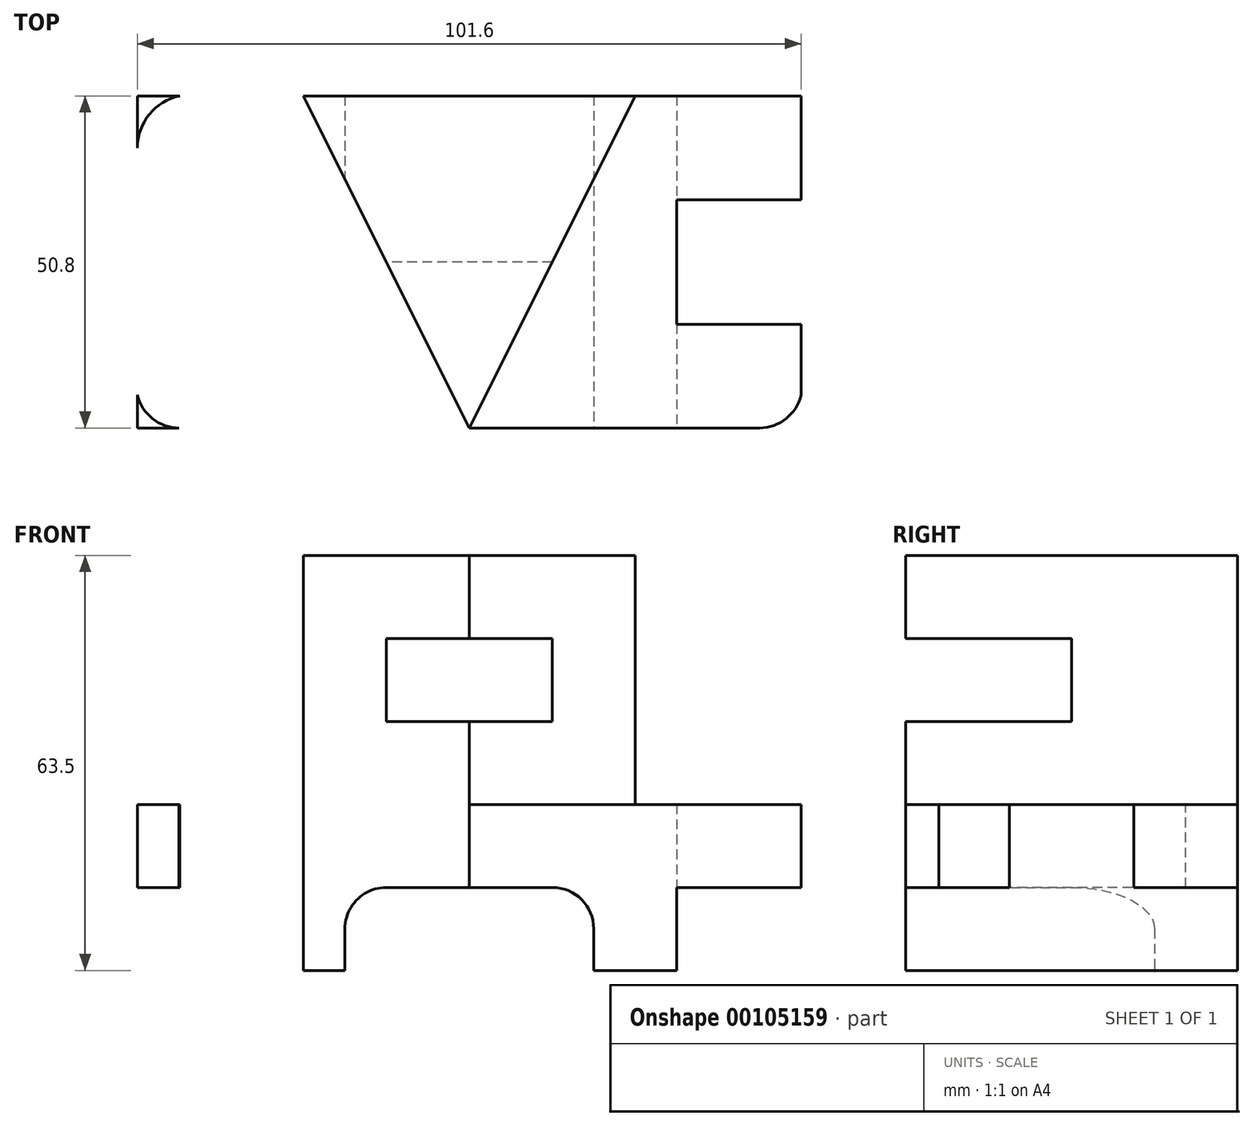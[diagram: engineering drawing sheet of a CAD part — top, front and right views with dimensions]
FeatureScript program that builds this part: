
annotation { "Feature Type Name" : "Feature", "Feature Type Description" : "" }
export const myFeature = defineFeature(function(context is Context, id is Id, definition is map)
    precondition{}
    {
        {
            var Q0;
            Q0=qCreatedBy(makeId("Top.planeOp"),FACE);
            var sketch = newSketch(context, id + "F0", { "sketchPlane" : qUnion([Q0])});
            skLineSegment(sketch, "E0.bottom", {"start": v(0, 0) * mm, "end": v(101.6, 0) * mm});
            skLineSegment(sketch, "E0.top", {"start": v(0, 50.8) * mm, "end": v(101.6, 50.8) * mm});
            skLineSegment(sketch, "E0.left", {"start": v(0, 0) * mm, "end": v(0, 50.8) * mm});
            skLineSegment(sketch, "E0.right", {"start": v(101.6, 0) * mm, "end": v(101.6, 50.8) * mm});
            skLineSegment(sketch, "E1.bottom", {"start": v(0, 34.92) * mm, "end": v(19.05, 34.92) * mm});
            skLineSegment(sketch, "E1.top", {"start": v(0, 15.88) * mm, "end": v(19.05, 15.88) * mm});
            skLineSegment(sketch, "E1.left", {"start": v(0, 34.92) * mm, "end": v(0, 15.88) * mm});
            skLineSegment(sketch, "E1.right", {"start": v(19.05, 34.92) * mm, "end": v(19.05, 15.88) * mm});
            skLineSegment(sketch, "E2.bottom", {"start": v(101.6, 34.93) * mm, "end": v(82.55, 34.93) * mm});
            skLineSegment(sketch, "E2.top", {"start": v(101.6, 15.88) * mm, "end": v(82.55, 15.88) * mm});
            skLineSegment(sketch, "E2.left", {"start": v(101.6, 34.93) * mm, "end": v(101.6, 15.88) * mm});
            skLineSegment(sketch, "E2.right", {"start": v(82.55, 34.93) * mm, "end": v(82.55, 15.88) * mm});
            skSolve(sketch);
        }
        {
            var Q0;
            {var subQ1=sQuery(id+"F0.wireOp",EDGE,"E0.bottom");Q0=makeQuery(id+"F0.imprint","IMPRINT",FACE,{"disambiguationData":[TD([[makeQuery(id+"F0.imprint","IMPRINT",EDGE,{"derivedFrom":subQ1}),1.0]])]});}
            extrude(context, id + "F1", {"entities" : qUnion([Q0]), "endBound" : BoundingType.SYMMETRIC, "depth" : 25.4 * mm});
        }
        {
            var Q0;
            Q0=makeQuery(id+"F1.opExtrude","CAP_FACE",FACE,{"disambiguationData":[OSD([sQuery(id+"F0.wireOp",EDGE,"E0.bottom"),sQuery(id+"F0.wireOp",EDGE,"E0.top"),sQuery(id+"F0.wireOp",EDGE,"E0.left"),sQuery(id+"F0.wireOp",EDGE,"E0.right"),sQuery(id+"F0.wireOp",EDGE,"E1.bottom"),sQuery(id+"F0.wireOp",EDGE,"E1.top"),sQuery(id+"F0.wireOp",EDGE,"E1.right"),sQuery(id+"F0.wireOp",EDGE,"E2.bottom"),sQuery(id+"F0.wireOp",EDGE,"E2.top"),sQuery(id+"F0.wireOp",EDGE,"E2.right")])],"isStart":false});
            var sketch = newSketch(context, id + "F2", { "sketchPlane" : qUnion([Q0])});
            skLineSegment(sketch, "E3.bottom", {"start": v(25.4, 50.8) * mm, "end": v(76.2, 50.8) * mm});
            skLineSegment(sketch, "E3.top", {"start": v(25.4, 0) * mm, "end": v(76.2, 0) * mm});
            skLineSegment(sketch, "E3.left", {"start": v(25.4, 50.8) * mm, "end": v(25.4, 0) * mm});
            skLineSegment(sketch, "E3.right", {"start": v(76.2, 50.8) * mm, "end": v(76.2, 0) * mm});
            skLineSegment(sketch, "E4", {"start": v(25.4, 50.8) * mm, "end": v(50.8, 0) * mm});
            skLineSegment(sketch, "E5", {"start": v(50.8, 0) * mm, "end": v(76.2, 50.8) * mm});
            skSolve(sketch);
        }
        {
            var Q0;
            Q0=makeQuery(id+"F2.imprint","IMPRINT",FACE,{"disambiguationData":[TD([[makeQuery(id+"F2.imprint","IMPRINT",EDGE,{"derivedFrom":sQuery(id+"F2.wireOp",EDGE,"E3.bottom")}),-1.0]])]});
            extrude(context, id + "F3", {"entities" : qUnion([Q0]), "operationType" : NewBodyOperationType.ADD, "depth" : 38.1 * mm});
        }
        {
            var Q0;
            Q0=makeQuery(id+"F1.opExtrude","SWEPT_FACE",FACE,{"disambiguationData":[OSD([sQuery(id+"F0.wireOp",EDGE,"E0.bottom")])]});
            var sketch = newSketch(context, id + "F4", { "sketchPlane" : qUnion([Q0])});
            skLineSegment(sketch, "E6.bottom", {"start": v(82.55, -12.7) * mm, "end": v(101.6, -12.7) * mm});
            skLineSegment(sketch, "E6.top", {"start": v(82.55, 0) * mm, "end": v(101.6, 0) * mm});
            skLineSegment(sketch, "E6.left", {"start": v(82.55, -12.7) * mm, "end": v(82.55, 0) * mm});
            skLineSegment(sketch, "E6.right", {"start": v(101.6, -12.7) * mm, "end": v(101.6, 0) * mm});
            skLineSegment(sketch, "E7.bottom", {"start": v(0, 0) * mm, "end": v(19.05, 0) * mm});
            skLineSegment(sketch, "E7.top", {"start": v(0, -12.7) * mm, "end": v(19.05, -12.7) * mm});
            skLineSegment(sketch, "E7.left", {"start": v(0, 0) * mm, "end": v(0, -12.7) * mm});
            skLineSegment(sketch, "E7.right", {"start": v(19.05, 0) * mm, "end": v(19.05, -12.7) * mm});
            skLineSegment(sketch, "E8.top", {"start": v(19.05, -12.7) * mm, "end": v(31.75, -12.7) * mm});
            skLineSegment(sketch, "E9.top", {"start": v(82.55, -12.7) * mm, "end": v(69.85, -12.7) * mm});
            skLineSegment(sketch, "E9.left", {"start": v(82.55, 0) * mm, "end": v(82.55, -12.7) * mm});
            skLineSegment(sketch, "E10.top", {"start": v(31.75, -12.7) * mm, "end": v(69.85, -12.7) * mm});
            skLineSegment(sketch, "E11", {"start": v(31.75, -12.7) * mm, "end": v(31.75, -6.35) * mm});
            skLineSegment(sketch, "E12", {"start": v(69.85, -12.7) * mm, "end": v(69.85, -6.35) * mm});
            skLineSegment(sketch, "E13", {"start": v(38.1, 0) * mm, "end": v(63.5, 0) * mm});
            skArc(sketch, "E14", {"start": v(31.75, -6.35) * mm, "mid": v(33.6, -1.86) * mm, "end": v(38.1, 0) * mm});
            skArc(sketch, "E15", {"start": v(63.5, 0) * mm, "mid": v(68, -1.86) * mm, "end": v(69.85, -6.35) * mm});
            skSolve(sketch);
        }
        {
            var Q0;
            Q0=makeQuery(id+"F4.imprint","IMPRINT",FACE,{"disambiguationData":[TD([[makeQuery(id+"F4.imprint","IMPRINT",EDGE,{"derivedFrom":sQuery(id+"F4.wireOp",EDGE,"E7.bottom")}),-1.0]])]});
            var Q1;
            Q1=makeQuery(id+"F4.imprint","IMPRINT",FACE,{"disambiguationData":[TD([[makeQuery(id+"F4.imprint","IMPRINT",EDGE,{"derivedFrom":sQuery(id+"F4.wireOp",EDGE,"E10.top")}),1.0]])]});
            var Q2;
            Q2=makeQuery(id+"F4.imprint","IMPRINT",FACE,{"disambiguationData":[TD([[makeQuery(id+"F4.imprint","IMPRINT",EDGE,{"derivedFrom":sQuery(id+"F4.wireOp",EDGE,"E6.bottom")}),1.0]])]});
            extrude(context, id + "F5", {"entities" : qUnion([Q0, Q1, Q2]), "operationType" : NewBodyOperationType.REMOVE, "endBound" : BoundingType.THROUGH_ALL, "oppositeDirection" : true, "depth" : 25.4 * mm});
        }
        {
            var Q0;
            Q0=makeQuery(id+"F3.boolean.opBoolean","MERGE",FACE,{"derivedFrom":[makeQuery(id+"F1.opExtrude","SWEPT_FACE",FACE,{"disambiguationData":[OSD([sQuery(id+"F0.wireOp",EDGE,"E0.top")])]}),makeQuery(id+"F3.opExtrude","SWEPT_FACE",FACE,{"disambiguationData":[OSD([sQuery(id+"F2.wireOp",EDGE,"E3.bottom")])]})]});
            var sketch = newSketch(context, id + "F6", { "sketchPlane" : qUnion([Q0])});
            skLineSegment(sketch, "E16.bottom", {"start": v(-63.5, 38.1) * mm, "end": v(-38.1, 38.1) * mm});
            skLineSegment(sketch, "E16.top", {"start": v(-63.5, 25.4) * mm, "end": v(-38.1, 25.4) * mm});
            skLineSegment(sketch, "E16.left", {"start": v(-63.5, 38.1) * mm, "end": v(-63.5, 25.4) * mm});
            skLineSegment(sketch, "E16.right", {"start": v(-38.1, 38.1) * mm, "end": v(-38.1, 25.4) * mm});
            skSolve(sketch);
        }
        {
            var Q0;
            Q0=makeQuery(id+"F6.imprint","IMPRINT",FACE,{"disambiguationData":[TD([[makeQuery(id+"F6.imprint","IMPRINT",EDGE,{"derivedFrom":sQuery(id+"F6.wireOp",EDGE,"E16.bottom")}),-1.0]])]});
            extrude(context, id + "F7", {"entities" : qUnion([Q0]), "operationType" : NewBodyOperationType.REMOVE, "oppositeDirection" : true, "depth" : 98.3 * mm, "hasSecondDirection" : true, "secondDirectionOppositeDirection" : true, "secondDirectionDepth" : 25.4 * mm});
        }
        {
            var Q0;
            {var subQ0=sQuery(id+"F0.wireOp",EDGE,"E1.top");var subQ1=sQuery(id+"F0.wireOp",EDGE,"E1.bottom");var subQ2=sQuery(id+"F0.wireOp",EDGE,"E0.bottom");var subQ3=sQuery(id+"F0.wireOp",EDGE,"E0.left");var subQ4=sQuery(id+"F0.wireOp",EDGE,"E0.top");var subQ6=sQuery(id+"F0.wireOp",EDGE,"E1.right");var subQ7=makeQuery(id+"F1.opExtrude","CAP_FACE",FACE,{"disambiguationData":[OSD([subQ2,subQ4,subQ3,sQuery(id+"F0.wireOp",EDGE,"E0.right"),subQ1,subQ0,subQ6,sQuery(id+"F0.wireOp",EDGE,"E2.bottom"),sQuery(id+"F0.wireOp",EDGE,"E2.top"),sQuery(id+"F0.wireOp",EDGE,"E2.right")])],"isStart":false});Q0=makeQuery(id+"F3.boolean.opBoolean","SPLIT",FACE,{"disambiguationData":[TD([makeQuery(id+"F1.opExtrude","SWEPT_FACE",FACE,{"disambiguationData":[OSD([subQ1])]})])],"derivedFrom":subQ7});}
            var sketch = newSketch(context, id + "F8", { "sketchPlane" : qUnion([Q0])});
            skLineSegment(sketch, "E17", {"start": v(0, 34.92) * mm, "end": v(0, 42.86) * mm});
            skLineSegment(sketch, "E18", {"start": v(0, 15.88) * mm, "end": v(0, 7.94) * mm});
            skLineSegment(sketch, "E19", {"start": v(6.35, 0) * mm, "end": v(48.54, 0) * mm});
            skLineSegment(sketch, "E20", {"start": v(6.48, 50.8) * mm, "end": v(25.4, 50.8) * mm});
            skArc(sketch, "E21", {"start": v(0, 42.86) * mm, "mid": v(1.82, 47.98) * mm, "end": v(6.48, 50.8) * mm});
            skArc(sketch, "E22", {"start": v(6.35, 0) * mm, "mid": v(1.27, 2.44) * mm, "end": v(0, 7.94) * mm});
            skSolve(sketch);
        }
        {
            var Q0;
            {var subQ0=sQuery(id+"F8.wireOp",EDGE,"E21");Q0=makeQuery(id+"F8.imprint","IMPRINT",FACE,{"disambiguationData":[TD([[makeQuery(id+"F8.imprint","IMPRINT",EDGE,{"derivedFrom":subQ0}),1.0]])]});}
            var Q1;
            {var subQ0=sQuery(id+"F8.wireOp",EDGE,"E22");var subQ1=sQuery(id+"F0.wireOp",EDGE,"E0.left");var subQ2=sQuery(id+"F0.wireOp",EDGE,"E0.bottom");var subQ4=makeQuery(id+"F0.imprint","IMPRINT",EDGE,{"disambiguationData":[TD([[makeQuery(id+"F0.imprint","INTERSECT",VERTEX,{"derivedFrom":[subQ2,subQ1]}),-1.0]])],"derivedFrom":subQ1});var subQ7=makeQuery(id+"F1.opExtrude","CAP_EDGE",EDGE,{"disambiguationData":[OSD([subQ1]),TDD([subQ4])],"isStart":false});var subQ8=makeQuery(id+"F8.imprint","INTERSECT",VERTEX,{"derivedFrom":[subQ7,subQ0]});Q1=makeQuery(id+"F8.imprint","IMPRINT",FACE,{"disambiguationData":[TD([[makeQuery(id+"F8.imprint","IMPRINT",EDGE,{"disambiguationData":[TD([[subQ8,1.0]])],"derivedFrom":subQ0}),1.0]])]});}
            extrude(context, id + "F9", {"entities" : qUnion([Q0, Q1]), "operationType" : NewBodyOperationType.REMOVE, "endBound" : BoundingType.THROUGH_ALL, "oppositeDirection" : true, "depth" : 25.4 * mm});
        }
        {
            var Q0;
            {var subQ0=sQuery(id+"F0.wireOp",EDGE,"E0.bottom");var subQ1=sQuery(id+"F0.wireOp",EDGE,"E2.top");var subQ2=sQuery(id+"F0.wireOp",EDGE,"E2.bottom");var subQ3=sQuery(id+"F0.wireOp",EDGE,"E0.right");var subQ4=sQuery(id+"F0.wireOp",EDGE,"E0.top");var subQ6=sQuery(id+"F0.wireOp",EDGE,"E2.right");var subQ7=makeQuery(id+"F1.opExtrude","CAP_FACE",FACE,{"disambiguationData":[OSD([subQ0,subQ4,sQuery(id+"F0.wireOp",EDGE,"E0.left"),subQ3,sQuery(id+"F0.wireOp",EDGE,"E1.bottom"),sQuery(id+"F0.wireOp",EDGE,"E1.top"),sQuery(id+"F0.wireOp",EDGE,"E1.right"),subQ2,subQ1,subQ6])],"isStart":false});Q0=makeQuery(id+"F3.boolean.opBoolean","SPLIT",FACE,{"disambiguationData":[TD([makeQuery(id+"F1.opExtrude","SWEPT_FACE",FACE,{"disambiguationData":[OSD([subQ2])]})])],"derivedFrom":subQ7});}
            var sketch = newSketch(context, id + "F10", { "sketchPlane" : qUnion([Q0])});
            skLineSegment(sketch, "E23", {"start": v(76.2, 50.8) * mm, "end": v(95.25, 50.8) * mm});
            skLineSegment(sketch, "E24", {"start": v(101.6, 34.93) * mm, "end": v(101.6, 42.86) * mm});
            skLineSegment(sketch, "E25", {"start": v(101.6, 0) * mm, "end": v(101.6, 7.94) * mm});
            skLineSegment(sketch, "E26", {"start": v(50.8, 0) * mm, "end": v(95.25, 0) * mm});
            skArc(sketch, "E27", {"start": v(95.25, 50.8) * mm, "mid": v(100.33, 48.36) * mm, "end": v(101.6, 42.86) * mm});
            skArc(sketch, "E28", {"start": v(95.25, 0) * mm, "mid": v(100.33, 2.44) * mm, "end": v(101.6, 7.94) * mm});
            skSolve(sketch);
        }
        {
            var Q0;
            {var subQ0=sQuery(id+"F10.wireOp",EDGE,"E27");var subQ1=sQuery(id+"F0.wireOp",EDGE,"E0.right");var subQ2=sQuery(id+"F0.wireOp",EDGE,"E0.top");var subQ4=makeQuery(id+"F0.imprint","IMPRINT",EDGE,{"disambiguationData":[TD([[makeQuery(id+"F0.imprint","INTERSECT",VERTEX,{"derivedFrom":[subQ2,subQ1]}),1.0]])],"derivedFrom":subQ1});var subQ7=makeQuery(id+"F1.opExtrude","CAP_EDGE",EDGE,{"disambiguationData":[OSD([subQ1]),TDD([subQ4])],"isStart":false});var subQ8=makeQuery(id+"F10.imprint","INTERSECT",VERTEX,{"derivedFrom":[subQ7,subQ0]});Q0=makeQuery(id+"F10.imprint","IMPRINT",FACE,{"disambiguationData":[TD([[makeQuery(id+"F10.imprint","IMPRINT",EDGE,{"disambiguationData":[TD([[subQ8,1.0]])],"derivedFrom":subQ0}),1.0]])]});}
            var Q1;
            {var subQ0=sQuery(id+"F10.wireOp",EDGE,"E25");var subQ6=sQuery(id+"F10.wireOp",EDGE,"E28");var subQ7=makeQuery(id+"F10.imprint","INTERSECT",VERTEX,{"derivedFrom":[subQ0,subQ6]});Q1=makeQuery(id+"F10.imprint","IMPRINT",FACE,{"disambiguationData":[TD([[makeQuery(id+"F10.imprint","IMPRINT",EDGE,{"disambiguationData":[TD([[subQ7,1.0]])],"derivedFrom":subQ0}),1.0]])]});}
            extrude(context, id + "F11", {"entities" : qUnion([Q0, Q1]), "operationType" : NewBodyOperationType.REMOVE, "endBound" : BoundingType.THROUGH_ALL, "oppositeDirection" : true, "depth" : 25.4 * mm});
        }
    });
